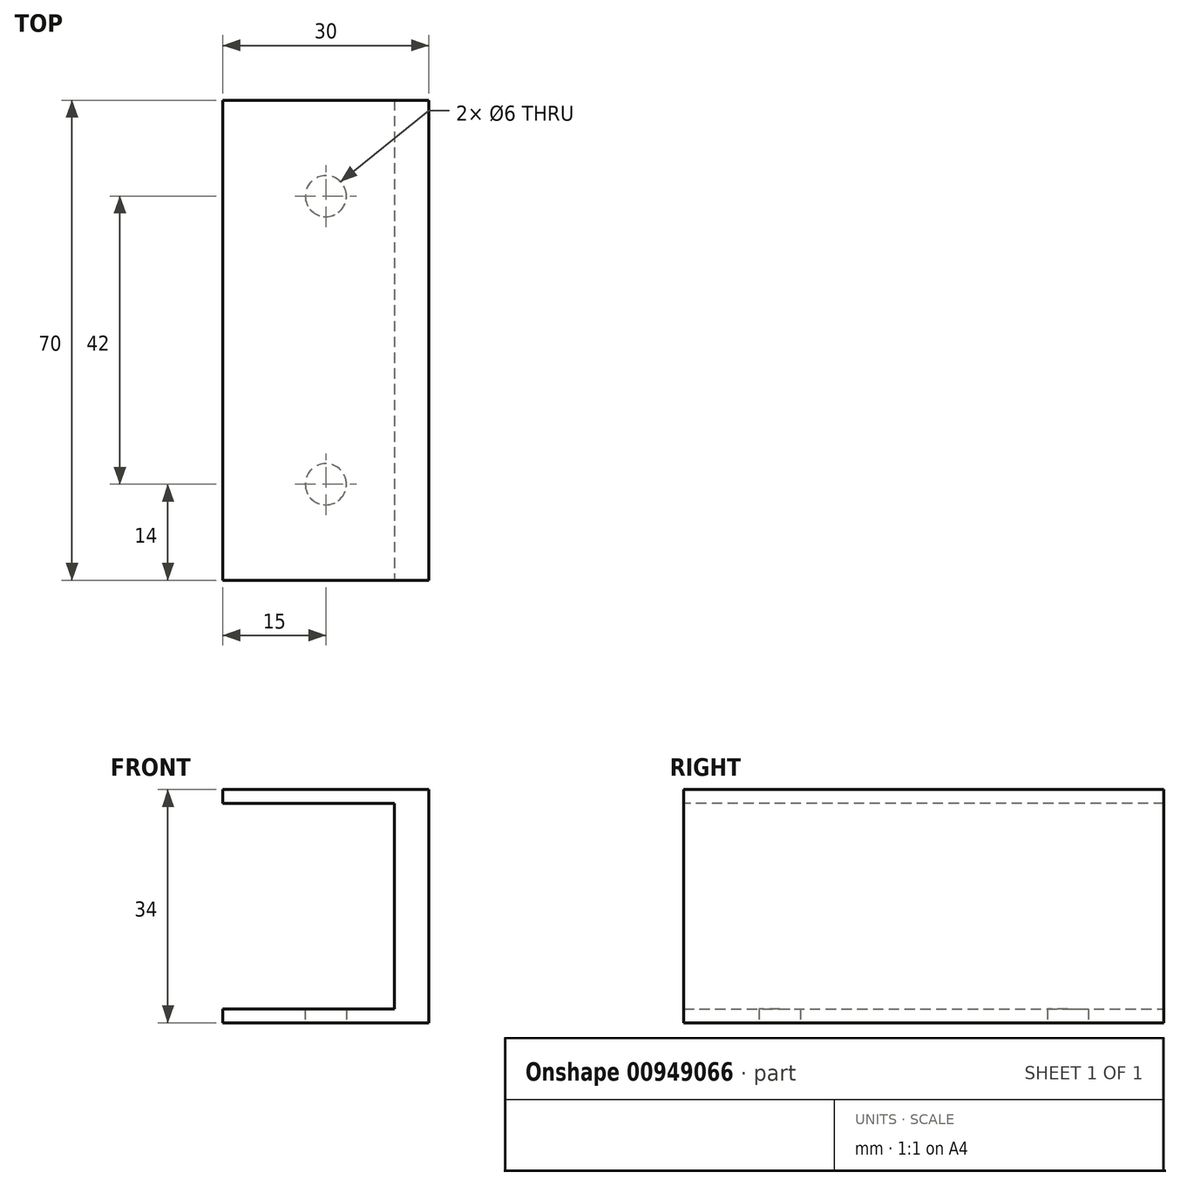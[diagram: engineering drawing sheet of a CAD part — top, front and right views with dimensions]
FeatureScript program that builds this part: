
annotation { "Feature Type Name" : "Feature", "Feature Type Description" : "" }
export const myFeature = defineFeature(function(context is Context, id is Id, definition is map)
    precondition{}
    {
        {
            var Q0;
            Q0=qCreatedBy(makeId("Top.planeOp"),FACE);
            var sketch = newSketch(context, id + "F0", { "sketchPlane" : qUnion([Q0])});
            skLineSegment(sketch, "E0.bottom", {"start": v(0, 0) * mm, "end": v(30, 0) * mm});
            skLineSegment(sketch, "E0.top", {"start": v(0, 70) * mm, "end": v(30, 70) * mm});
            skLineSegment(sketch, "E0.left", {"start": v(0, 0) * mm, "end": v(0, 70) * mm});
            skLineSegment(sketch, "E0.right", {"start": v(30, 0) * mm, "end": v(30, 70) * mm});
            skSolve(sketch);
        }
        {
            var Q0;
            Q0 = qSketchRegion(id + "F0", true);
            extrude(context, id + "F1", {"entities" : qUnion([Q0]), "depth" : 2 * mm, "offsetDistance" : 25 * mm});
        }
        {
            var Q0;
            Q0=makeQuery(id+"F1.opExtrude","CAP_FACE",FACE,{"disambiguationData":[OSD([sQuery(id+"F0.wireOp",EDGE,"E0.bottom"),sQuery(id+"F0.wireOp",EDGE,"E0.top"),sQuery(id+"F0.wireOp",EDGE,"E0.left"),sQuery(id+"F0.wireOp",EDGE,"E0.right")])],"isStart":false});
            var sketch = newSketch(context, id + "F2", { "sketchPlane" : qUnion([Q0])});
            skLineSegment(sketch, "E1.bottom", {"start": v(30, 70) * mm, "end": v(25, 70) * mm});
            skLineSegment(sketch, "E1.top", {"start": v(30, 0) * mm, "end": v(25, 0) * mm});
            skLineSegment(sketch, "E1.left", {"start": v(30, 70) * mm, "end": v(30, 0) * mm});
            skLineSegment(sketch, "E1.right", {"start": v(25, 70) * mm, "end": v(25, 0) * mm});
            skSolve(sketch);
        }
        {
            var Q0;
            Q0 = qSketchRegion(id + "F2", true);
            extrude(context, id + "F3", {"entities" : qUnion([Q0]), "operationType" : NewBodyOperationType.ADD, "depth" : 30 * mm, "offsetDistance" : 25 * mm});
        }
        {
            var Q0;
            Q0=makeQuery(id+"F3.opExtrude","CAP_FACE",FACE,{"disambiguationData":[OSD([sQuery(id+"F2.wireOp",EDGE,"E1.bottom"),sQuery(id+"F2.wireOp",EDGE,"E1.top"),sQuery(id+"F2.wireOp",EDGE,"E1.left"),sQuery(id+"F2.wireOp",EDGE,"E1.right")])],"isStart":false});
            var sketch = newSketch(context, id + "F4", { "sketchPlane" : qUnion([Q0])});
            skLineSegment(sketch, "E2.bottom", {"start": v(30, 70) * mm, "end": v(0, 70) * mm});
            skLineSegment(sketch, "E2.top", {"start": v(30, 0) * mm, "end": v(0, 0) * mm});
            skLineSegment(sketch, "E2.left", {"start": v(30, 70) * mm, "end": v(30, 0) * mm});
            skLineSegment(sketch, "E2.right", {"start": v(0, 70) * mm, "end": v(0, 0) * mm});
            skSolve(sketch);
        }
        {
            var Q0;
            Q0 = qSketchRegion(id + "F4", true);
            extrude(context, id + "F5", {"entities" : qUnion([Q0]), "operationType" : NewBodyOperationType.ADD, "depth" : 2 * mm, "offsetDistance" : 25 * mm});
        }
        {
            var Q0;
            Q0=makeQuery(id+"F1.opExtrude","CAP_FACE",FACE,{"disambiguationData":[OSD([sQuery(id+"F0.wireOp",EDGE,"E0.bottom"),sQuery(id+"F0.wireOp",EDGE,"E0.top"),sQuery(id+"F0.wireOp",EDGE,"E0.left"),sQuery(id+"F0.wireOp",EDGE,"E0.right")])],"isStart":true});
            var sketch = newSketch(context, id + "F6", { "sketchPlane" : qUnion([Q0])});
            skLineSegment(sketch, "E3", {"start": v(15, 0) * mm, "end": v(15, -14) * mm});
            skLineSegment(sketch, "E4", {"start": v(15, -14) * mm, "end": v(15, -56) * mm});
            skCircle(sketch, "E5", {"center": v(15, -14) * mm, "radius": 3 * mm});
            skCircle(sketch, "E6", {"center": v(15, -56) * mm, "radius": 3 * mm});
            skSolve(sketch);
        }
        {
            var Q0;
            Q0 = qSketchRegion(id + "F6", true);
            extrude(context, id + "F7", {"entities" : qUnion([Q0]), "operationType" : NewBodyOperationType.REMOVE, "oppositeDirection" : true, "depth" : 5 * mm, "offsetDistance" : 25 * mm});
        }
    });
